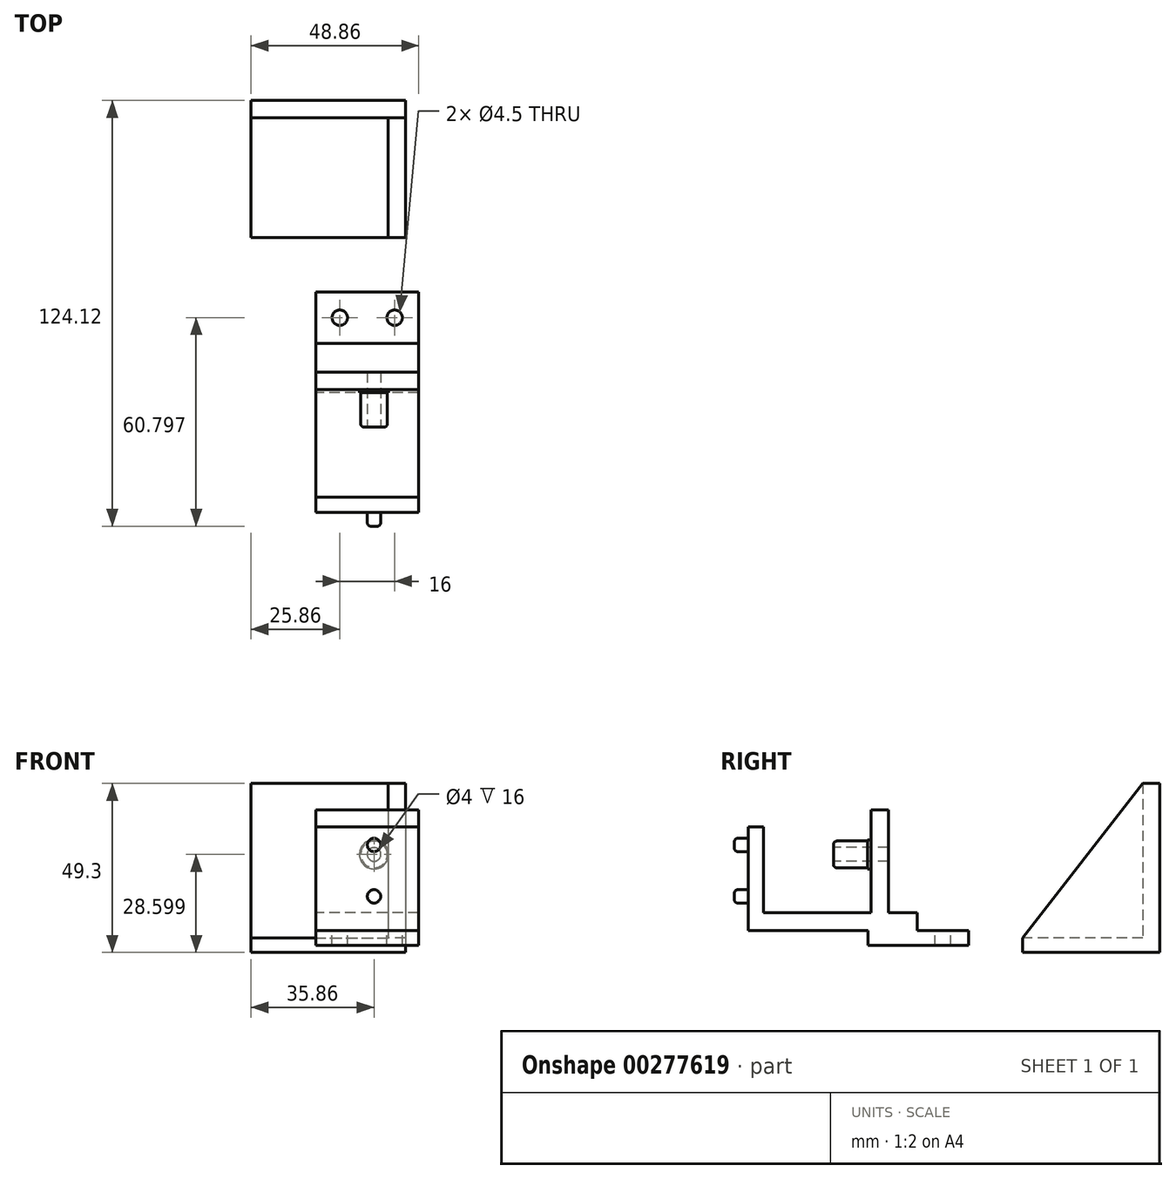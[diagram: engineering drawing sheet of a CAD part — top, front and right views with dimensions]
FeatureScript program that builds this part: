
annotation { "Feature Type Name" : "Feature", "Feature Type Description" : "" }
export const myFeature = defineFeature(function(context is Context, id is Id, definition is map)
    precondition{}
    {
        {
            var Q0;
            Q0=qCreatedBy(makeId("Top.planeOp"),FACE);
            var sketch = newSketch(context, id + "F0", { "sketchPlane" : qUnion([Q0])});
            skLineSegment(sketch, "E0.bottom", {"start": v(-18.86, 29.82) * mm, "end": v(21.14, 29.82) * mm});
            skLineSegment(sketch, "E0.top", {"start": v(-18.86, -10.18) * mm, "end": v(21.14, -10.18) * mm});
            skLineSegment(sketch, "E0.left", {"start": v(-18.86, 29.82) * mm, "end": v(-18.86, -10.18) * mm});
            skLineSegment(sketch, "E0.right", {"start": v(21.14, 29.82) * mm, "end": v(21.14, -10.18) * mm});
            skSolve(sketch);
        }
        {
            var Q0;
            Q0=makeQuery(id+"F0.imprint","IMPRINT",FACE,{"disambiguationData":[TD([[makeQuery(id+"F0.imprint","IMPRINT",EDGE,{"derivedFrom":sQuery(id+"F0.wireOp",EDGE,"E0.bottom")}),-1.0]])]});
            extrude(context, id + "F1", {"entities" : qUnion([Q0]), "depth" : 4.3 * mm});
        }
        {
            var Q0;
            Q0=makeQuery(id+"F1.opExtrude","CAP_FACE",FACE,{"disambiguationData":[OSD([sQuery(id+"F0.wireOp",EDGE,"E0.bottom"),sQuery(id+"F0.wireOp",EDGE,"E0.top"),sQuery(id+"F0.wireOp",EDGE,"E0.left"),sQuery(id+"F0.wireOp",EDGE,"E0.right")])],"isStart":false});
            var sketch = newSketch(context, id + "F2", { "sketchPlane" : qUnion([Q0])});
            skLineSegment(sketch, "E1.bottom", {"start": v(-18.86, 29.82) * mm, "end": v(21.14, 29.82) * mm});
            skLineSegment(sketch, "E1.top", {"start": v(-18.86, 24.82) * mm, "end": v(21.14, 24.82) * mm});
            skLineSegment(sketch, "E1.left", {"start": v(-18.86, 29.82) * mm, "end": v(-18.86, 24.82) * mm});
            skLineSegment(sketch, "E1.right", {"start": v(21.14, 29.82) * mm, "end": v(21.14, 24.82) * mm});
            skSolve(sketch);
        }
        {
            var Q0;
            Q0=makeQuery(id+"F2.imprint","IMPRINT",FACE,{"disambiguationData":[TD([[makeQuery(id+"F2.imprint","IMPRINT",EDGE,{"derivedFrom":sQuery(id+"F2.wireOp",EDGE,"E1.bottom")}),-1.0]])]});
            extrude(context, id + "F3", {"entities" : qUnion([Q0]), "operationType" : NewBodyOperationType.ADD, "depth" : 45 * mm});
        }
        {
            var Q0;
            Q0=makeQuery(id+"F3.boolean.opBoolean","MERGE",FACE,{"derivedFrom":[makeQuery(id+"F1.opExtrude","SWEPT_FACE",FACE,{"disambiguationData":[OSD([sQuery(id+"F0.wireOp",EDGE,"E0.right")])]}),makeQuery(id+"F3.opExtrude","SWEPT_FACE",FACE,{"disambiguationData":[OSD([sQuery(id+"F2.wireOp",EDGE,"E1.right")])]})]});
            var sketch = newSketch(context, id + "F4", { "sketchPlane" : qUnion([Q0])});
            skLineSegment(sketch, "E2", {"start": v(29.82, 49.3) * mm, "end": v(24.82, 49.3) * mm});
            skLineSegment(sketch, "E3", {"start": v(24.82, 49.3) * mm, "end": v(-10.18, 4.3) * mm});
            skLineSegment(sketch, "E4", {"start": v(-10.18, 4.3) * mm, "end": v(-10.18, 0) * mm});
            skLineSegment(sketch, "E5", {"start": v(-10.18, 0) * mm, "end": v(29.82, 0) * mm});
            skLineSegment(sketch, "E6", {"start": v(29.82, 0) * mm, "end": v(29.82, 49.3) * mm});
            skSolve(sketch);
        }
        {
            var Q0;
            Q0 = qSketchRegion(id + "F4", true);
            extrude(context, id + "F5", {"entities" : qUnion([Q0]), "operationType" : NewBodyOperationType.ADD, "depth" : 5 * mm});
        }
        {
            var Q0;
            Q0=qCreatedBy(makeId("Right.planeOp"),FACE);
            var sketch = newSketch(context, id + "F6", { "sketchPlane" : qUnion([Q0])});
            skLineSegment(sketch, "E7", {"start": v(-26, 2.03) * mm, "end": v(-55.3, 2.03) * mm});
            skLineSegment(sketch, "E8", {"start": v(-90.3, 6.37) * mm, "end": v(-90.3, 11.6) * mm});
            skLineSegment(sketch, "E9", {"start": v(-85.82, 11.6) * mm, "end": v(-54.4, 11.6) * mm});
            skLineSegment(sketch, "E10", {"start": v(-54.4, 11.6) * mm, "end": v(-54.4, 41.6) * mm});
            skLineSegment(sketch, "E11", {"start": v(-54.4, 41.6) * mm, "end": v(-49.4, 41.6) * mm});
            skLineSegment(sketch, "E12", {"start": v(-49.4, 41.6) * mm, "end": v(-49.4, 11.6) * mm});
            skLineSegment(sketch, "E13", {"start": v(-49.4, 11.6) * mm, "end": v(-41, 11.6) * mm});
            skLineSegment(sketch, "E14", {"start": v(-41, 11.6) * mm, "end": v(-41, 6.37) * mm});
            skLineSegment(sketch, "E15", {"start": v(-41, 6.37) * mm, "end": v(-26, 6.37) * mm});
            skLineSegment(sketch, "E16", {"start": v(-26, 6.37) * mm, "end": v(-26, 2.03) * mm});
            skPoint(sketch, "E17.start.orphan", {"position": v(-49.4, 6.37) * mm});
            skLineSegment(sketch, "E18", {"start": v(-90.3, 6.37) * mm, "end": v(-55.3, 6.37) * mm});
            skLineSegment(sketch, "E19", {"start": v(-55.3, 6.37) * mm, "end": v(-55.3, 2.03) * mm});
            skLineSegment(sketch, "E20", {"start": v(-90.3, 11.6) * mm, "end": v(-90.3, 36.6) * mm});
            skLineSegment(sketch, "E21", {"start": v(-90.3, 36.6) * mm, "end": v(-85.82, 36.6) * mm});
            skLineSegment(sketch, "E22", {"start": v(-85.82, 36.6) * mm, "end": v(-85.82, 11.6) * mm});
            skSolve(sketch);
        }
        {
            var Q0;
            Q0=makeQuery(id+"F6.imprint","IMPRINT",FACE,{"disambiguationData":[TD([[makeQuery(id+"F6.imprint","IMPRINT",EDGE,{"derivedFrom":sQuery(id+"F6.wireOp",EDGE,"E7")}),-1.0]])]});
            extrude(context, id + "F7", {"entities" : qUnion([Q0]), "depth" : 30 * mm});
        }
        {
            var Q0;
            Q0=makeQuery(id+"F7.opExtrude","SWEPT_FACE",FACE,{"disambiguationData":[OSD([sQuery(id+"F6.wireOp",EDGE,"E12")])]});
            var sketch = newSketch(context, id + "F8", { "sketchPlane" : qUnion([Q0])});
            skCircle(sketch, "E23", {"center": v(-17, 28.6) * mm, "radius": 4.25 * mm});
            skSolve(sketch);
        }
        {
            var Q0;
            Q0=makeQuery(id+"F8.imprint","IMPRINT",FACE,{"disambiguationData":[TD([[makeQuery(id+"F8.imprint","IMPRINT",EDGE,{"derivedFrom":sQuery(id+"F8.wireOp",EDGE,"E23")}),1.0]])]});
            extrude(context, id + "F9", {"entities" : qUnion([Q0]), "operationType" : NewBodyOperationType.ADD, "oppositeDirection" : true, "depth" : 6 * mm});
        }
        {
            var Q0;
            Q0=makeQuery(id+"F9.opExtrude","CAP_FACE",FACE,{"disambiguationData":[OSD([sQuery(id+"F8.wireOp",EDGE,"E23")])],"isStart":false});
            var sketch = newSketch(context, id + "F10", { "sketchPlane" : qUnion([Q0])});
            skCircle(sketch, "E24", {"center": v(17, 28.6) * mm, "radius": 3.9 * mm});
            skSolve(sketch);
        }
        {
            var Q0;
            Q0=makeQuery(id+"F10.imprint","IMPRINT",FACE,{"disambiguationData":[TD([[makeQuery(id+"F10.imprint","IMPRINT",EDGE,{"derivedFrom":sQuery(id+"F10.wireOp",EDGE,"E24")}),1.0]])]});
            extrude(context, id + "F11", {"entities" : qUnion([Q0]), "operationType" : NewBodyOperationType.ADD, "depth" : 10 * mm});
        }
        {
            var Q0;
            Q0=makeQuery(id+"F11.opExtrude","CAP_EDGE",EDGE,{"disambiguationData":[OSD([sQuery(id+"F10.wireOp",EDGE,"E24")])],"isStart":false});
            fillet(context, id + "F12", {"entities" : qUnion([Q0]), "radius" : 1 * mm, "tangentPropagation" : true, "allowEdgeOverflow" : false});
        }
        {
            var Q0;
            Q0=makeQuery(id+"F7.opExtrude","SWEPT_FACE",FACE,{"disambiguationData":[OSD([sQuery(id+"F6.wireOp",EDGE,"E15")])]});
            var sketch = newSketch(context, id + "F13", { "sketchPlane" : qUnion([Q0])});
            skLineSegment(sketch, "E25", {"start": v(30, -33.5) * mm, "end": v(0, -33.5) * mm, "construction": true});
            skCircle(sketch, "E26", {"center": v(23, -33.5) * mm, "radius": 2.25 * mm});
            skCircle(sketch, "E27", {"center": v(7, -33.5) * mm, "radius": 2.25 * mm});
            skSolve(sketch);
        }
        {
            var Q0;
            Q0 = qSketchRegion(id + "F13", true);
            extrude(context, id + "F14", {"entities" : qUnion([Q0]), "operationType" : NewBodyOperationType.REMOVE, "endBound" : BoundingType.UP_TO_NEXT, "oppositeDirection" : true, "depth" : 25 * mm});
        }
        {
            var Q0;
            Q0=makeQuery(id+"F11.opExtrude","CAP_FACE",FACE,{"disambiguationData":[OSD([sQuery(id+"F10.wireOp",EDGE,"E24")])],"isStart":false});
            var sketch = newSketch(context, id + "F15", { "sketchPlane" : qUnion([Q0])});
            skCircle(sketch, "E28", {"center": v(17, 28.6) * mm, "radius": 2 * mm});
            skSolve(sketch);
        }
        {
            var Q0;
            Q0=makeQuery(id+"F15.imprint","IMPRINT",FACE,{"disambiguationData":[TD([[makeQuery(id+"F15.imprint","IMPRINT",EDGE,{"derivedFrom":sQuery(id+"F15.wireOp",EDGE,"E28")}),1.0]])]});
            extrude(context, id + "F16", {"entities" : qUnion([Q0]), "operationType" : NewBodyOperationType.REMOVE, "endBound" : BoundingType.UP_TO_NEXT, "oppositeDirection" : true, "depth" : 5 * mm});
        }
        {
            var Q0;
            Q0=makeQuery(id+"F7.opExtrude","SWEPT_FACE",FACE,{"disambiguationData":[OSD([sQuery(id+"F6.wireOp",EDGE,"E8"),sQuery(id+"F6.wireOp",EDGE,"E20")])]});
            var sketch = newSketch(context, id + "F17", { "sketchPlane" : qUnion([Q0])});
            skCircle(sketch, "E29", {"center": v(17, 16.37) * mm, "radius": 1.95 * mm});
            skCircle(sketch, "E30", {"center": v(17, 31.37) * mm, "radius": 1.95 * mm});
            skLineSegment(sketch, "E31", {"start": v(17, 16.37) * mm, "end": v(17, 33.25) * mm, "construction": true});
            skSolve(sketch);
        }
        {
            var Q0;
            Q0=makeQuery(id+"F17.imprint","IMPRINT",FACE,{"disambiguationData":[TD([[makeQuery(id+"F17.imprint","IMPRINT",EDGE,{"derivedFrom":sQuery(id+"F17.wireOp",EDGE,"E30")}),1.0]])]});
            var Q1;
            Q1=makeQuery(id+"F17.imprint","IMPRINT",FACE,{"disambiguationData":[TD([[makeQuery(id+"F17.imprint","IMPRINT",EDGE,{"derivedFrom":sQuery(id+"F17.wireOp",EDGE,"E29")}),1.0]])]});
            extrude(context, id + "F18", {"entities" : qUnion([Q0, Q1]), "operationType" : NewBodyOperationType.ADD, "depth" : 4 * mm});
        }
        {
            var Q0;
            Q0=makeQuery(id+"F18.opExtrude","CAP_EDGE",EDGE,{"disambiguationData":[OSD([sQuery(id+"F17.wireOp",EDGE,"E30")])],"isStart":false});
            var Q1;
            Q1=makeQuery(id+"F18.opExtrude","CAP_EDGE",EDGE,{"disambiguationData":[OSD([sQuery(id+"F17.wireOp",EDGE,"E29")])],"isStart":false});
            fillet(context, id + "F19", {"entities" : qUnion([Q0, Q1]), "radius" : 1 * mm, "tangentPropagation" : true, "allowEdgeOverflow" : false});
        }
    });
